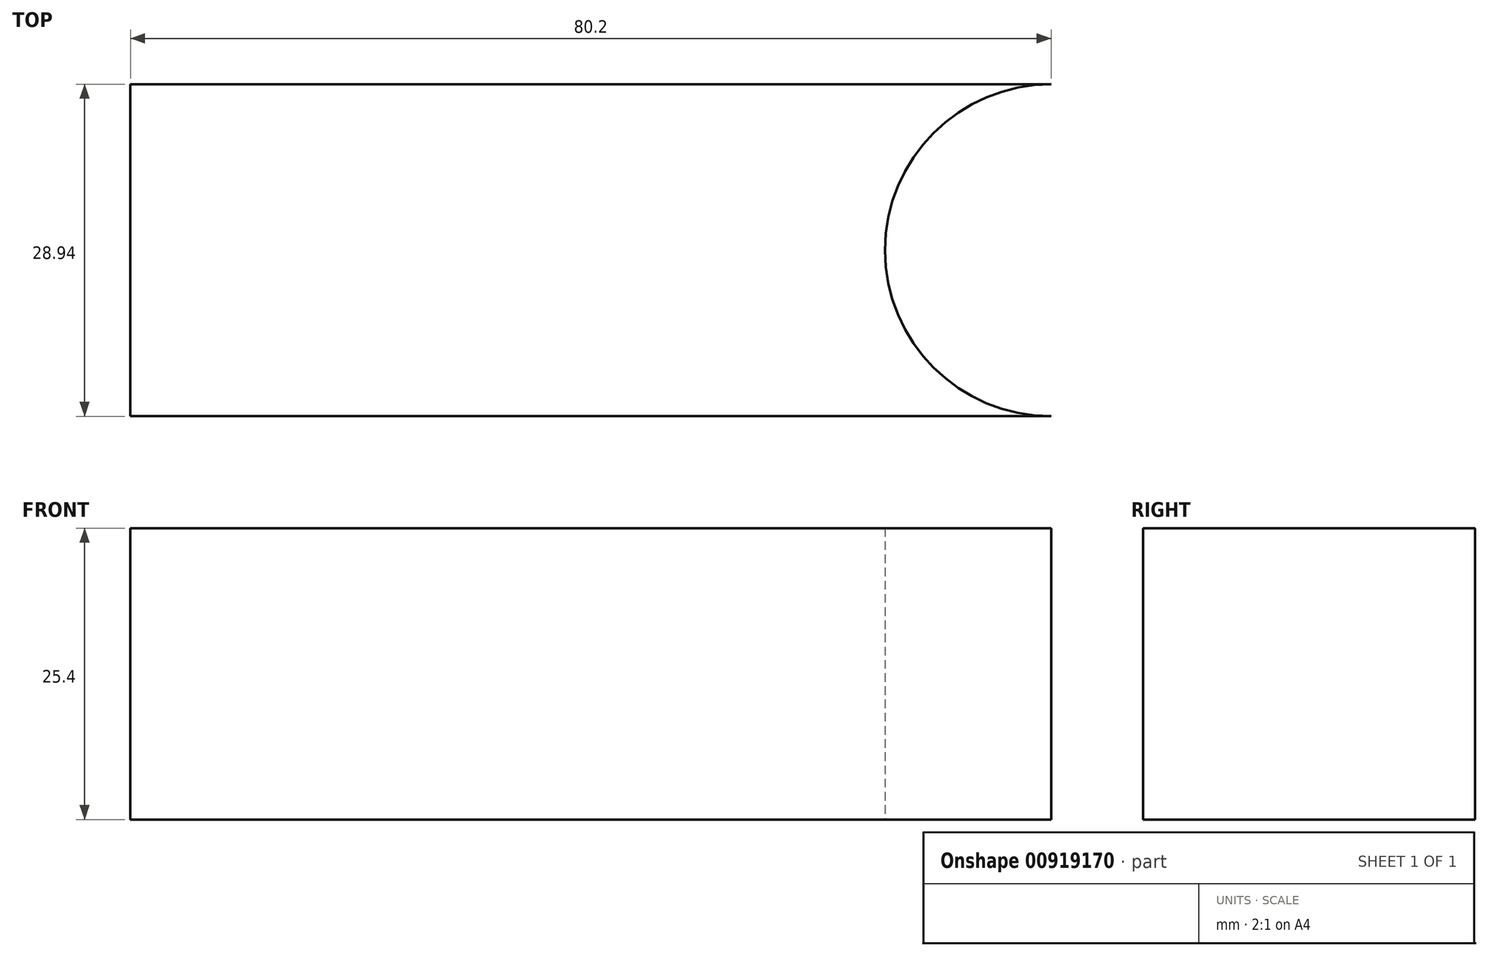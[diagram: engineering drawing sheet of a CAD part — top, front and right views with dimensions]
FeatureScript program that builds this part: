
annotation { "Feature Type Name" : "Feature", "Feature Type Description" : "" }
export const myFeature = defineFeature(function(context is Context, id is Id, definition is map)
    precondition{}
    {
        {
            var Q0;
            Q0=qCreatedBy(makeId("Top.planeOp"),FACE);
            var sketch = newSketch(context, id + "F0", { "sketchPlane" : qUnion([Q0])});
            skLineSegment(sketch, "E0.bottom", {"start": v(-40.1, -14.47) * mm, "end": v(40.1, -14.47) * mm});
            skLineSegment(sketch, "E0.top", {"start": v(-40.1, 14.47) * mm, "end": v(40.1, 14.47) * mm});
            skLineSegment(sketch, "E0.left", {"start": v(-40.1, -14.47) * mm, "end": v(-40.1, 14.47) * mm});
            skLineSegment(sketch, "E0.right", {"start": v(40.1, -14.47) * mm, "end": v(40.1, 14.47) * mm});
            skPoint(sketch, "E0.middle", {"position": v(0, 0) * mm});
            skCircle(sketch, "E1", {"center": v(40.1, 0) * mm, "radius": 14.47 * mm});
            skSolve(sketch);
        }
        {
            var Q0;
            {var subQ0=sQuery(id+"F0.wireOp",EDGE,"E0.bottom");Q0=makeQuery(id+"F0.imprint","IMPRINT",FACE,{"disambiguationData":[TD([[makeQuery(id+"F0.imprint","IMPRINT",EDGE,{"derivedFrom":subQ0}),1.0]])]});}
            extrude(context, id + "F1", {"entities" : qUnion([Q0]), "depth" : 25.4 * mm, "offsetDistance" : 25.4 * mm});
        }
    });
